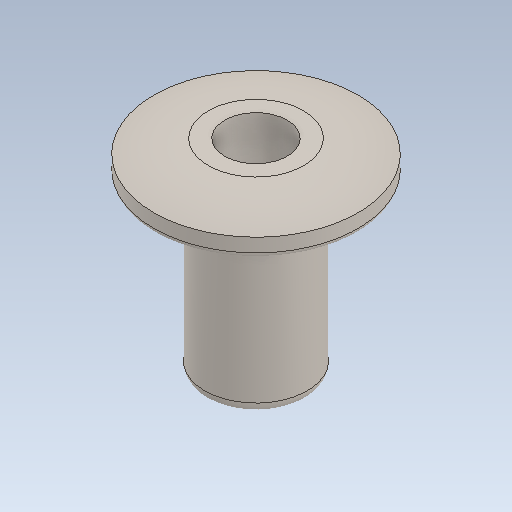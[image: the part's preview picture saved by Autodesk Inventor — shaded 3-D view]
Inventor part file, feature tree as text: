
AUTODESK INVENTOR PART (.ipt)
format: ipt  version: 2020.2 (Build 242310000, 310)  size: 134,656 bytes
history: native  units: in
note: dims shown in document units (in); Inventor stores cm internally (conversion verified against a paired STEP export)
features: fillet x1
ambient origin geometry x8: Origin, YZ Plane, XZ Plane, XY Plane, X Axis, Y Axis, Z Axis, Center Point
bodies: Solid1 (feature_tree)
feature tree (1):
  fillet  "Fillet1"  [1 undecoded]
note: 1 required parameter value undecoded (feature->parameter linkage not recoverable at this tier; creation-order binding heuristic only, values carry confidence <= 0.55)
